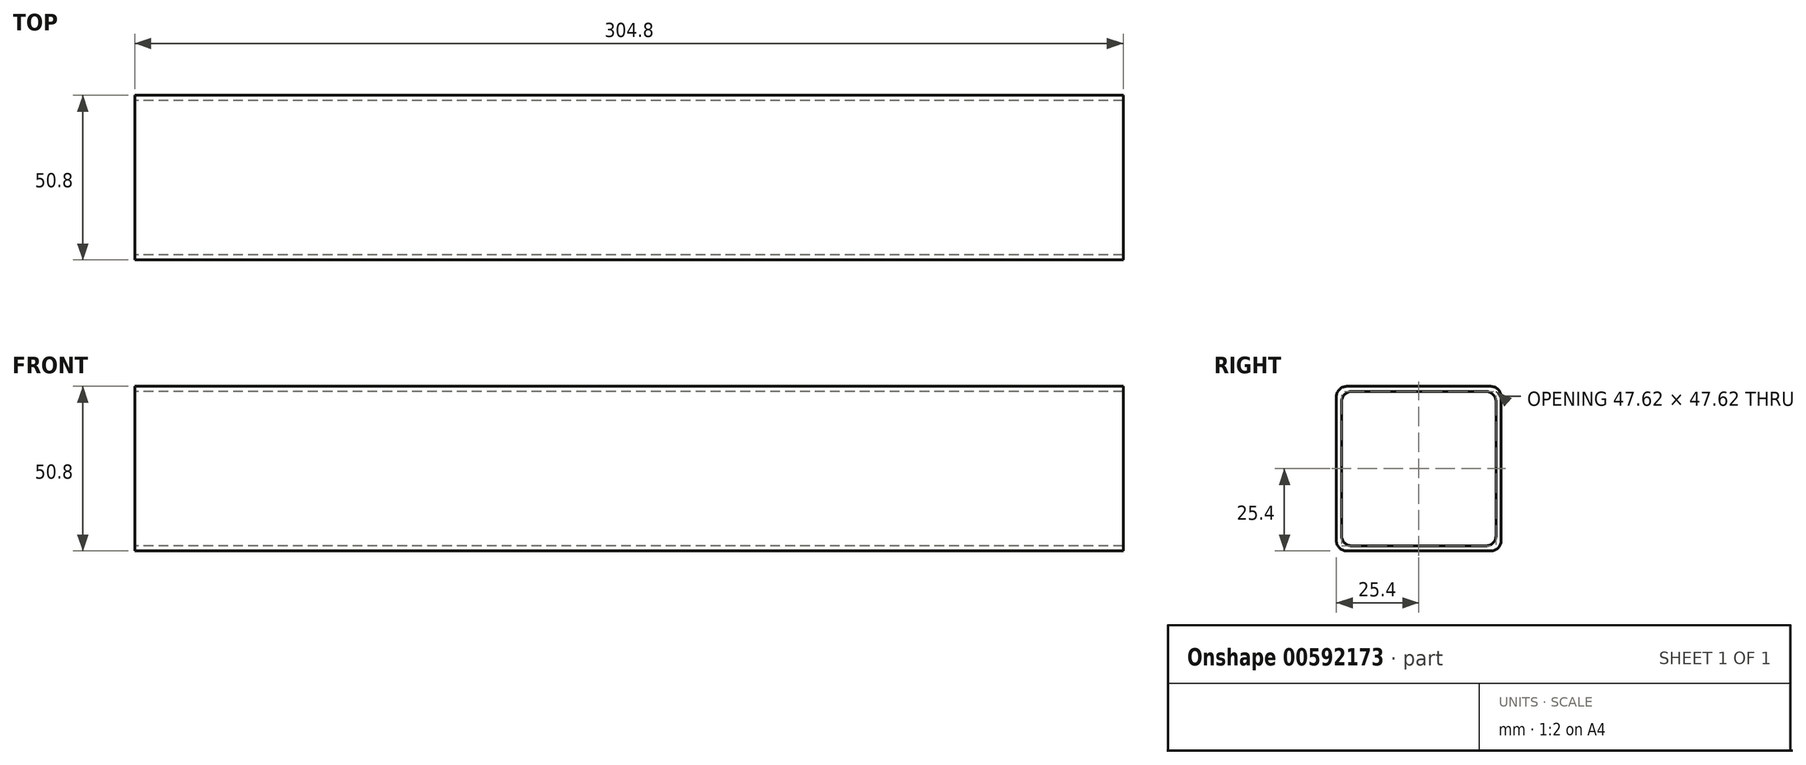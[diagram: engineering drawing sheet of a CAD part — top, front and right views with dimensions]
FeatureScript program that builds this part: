
annotation { "Feature Type Name" : "Feature", "Feature Type Description" : "" }
export const myFeature = defineFeature(function(context is Context, id is Id, definition is map)
    precondition{}
    {
        {
            var Q0;
            Q0=qCreatedBy(makeId("Right.planeOp"),FACE);
            var sketch = newSketch(context, id + "F0", { "sketchPlane" : qUnion([Q0])});
            skLineSegment(sketch, "E0.bottom", {"start": v(22.23, 25.4) * mm, "end": v(-22.22, 25.4) * mm});
            skLineSegment(sketch, "E0.top", {"start": v(22.22, -25.4) * mm, "end": v(-22.23, -25.4) * mm});
            skLineSegment(sketch, "E0.left", {"start": v(25.4, 22.22) * mm, "end": v(25.4, -22.22) * mm});
            skLineSegment(sketch, "E0.right", {"start": v(-25.4, 22.23) * mm, "end": v(-25.4, -22.22) * mm});
            skPoint(sketch, "E0.middle", {"position": v(0, 0) * mm});
            skLineSegment(sketch, "E1.0", {"start": v(20.64, 23.81) * mm, "end": v(-20.64, 23.81) * mm});
            skLineSegment(sketch, "E1.1", {"start": v(23.81, 20.64) * mm, "end": v(23.81, -20.64) * mm});
            skLineSegment(sketch, "E1.2", {"start": v(20.64, -23.81) * mm, "end": v(-20.64, -23.81) * mm});
            skLineSegment(sketch, "E1.3", {"start": v(-23.81, 20.64) * mm, "end": v(-23.81, -20.64) * mm});
            skPoint(sketch, "E2.visualSharp", {"position": v(-23.81, 23.81) * mm});
            skArc(sketch, "E2.filletArc", {"start": v(-20.64, 23.81) * mm, "mid": v(-22.88, 22.88) * mm, "end": v(-23.81, 20.64) * mm});
            skPoint(sketch, "E3.visualSharp", {"position": v(23.81, 23.81) * mm});
            skArc(sketch, "E3.filletArc", {"start": v(23.81, 20.64) * mm, "mid": v(22.88, 22.88) * mm, "end": v(20.64, 23.81) * mm});
            skPoint(sketch, "E4.visualSharp", {"position": v(-23.81, -23.81) * mm});
            skArc(sketch, "E4.filletArc", {"start": v(-23.81, -20.64) * mm, "mid": v(-22.88, -22.88) * mm, "end": v(-20.64, -23.81) * mm});
            skPoint(sketch, "E5.visualSharp", {"position": v(23.81, -23.81) * mm});
            skArc(sketch, "E5.filletArc", {"start": v(20.64, -23.81) * mm, "mid": v(22.88, -22.88) * mm, "end": v(23.81, -20.64) * mm});
            skPoint(sketch, "E6.visualSharp", {"position": v(25.4, -25.4) * mm});
            skArc(sketch, "E6.filletArc", {"start": v(22.22, -25.4) * mm, "mid": v(24.47, -24.47) * mm, "end": v(25.4, -22.22) * mm});
            skPoint(sketch, "E7.visualSharp", {"position": v(-25.4, -25.4) * mm});
            skArc(sketch, "E7.filletArc", {"start": v(-25.4, -22.22) * mm, "mid": v(-24.47, -24.47) * mm, "end": v(-22.23, -25.4) * mm});
            skPoint(sketch, "E8.visualSharp", {"position": v(-25.4, 25.4) * mm});
            skArc(sketch, "E8.filletArc", {"start": v(-22.22, 25.4) * mm, "mid": v(-24.47, 24.47) * mm, "end": v(-25.4, 22.23) * mm});
            skPoint(sketch, "E9.visualSharp", {"position": v(25.4, 25.4) * mm});
            skArc(sketch, "E9.filletArc", {"start": v(25.4, 22.22) * mm, "mid": v(24.47, 24.47) * mm, "end": v(22.23, 25.4) * mm});
            skSolve(sketch);
        }
        {
            var Q0;
            Q0 = qSketchRegion(id + "F0", true);
            extrude(context, id + "F1", {"entities" : qUnion([Q0]), "depth" : 304.8 * mm, "offsetDistance" : 25.4 * mm});
        }
    });
